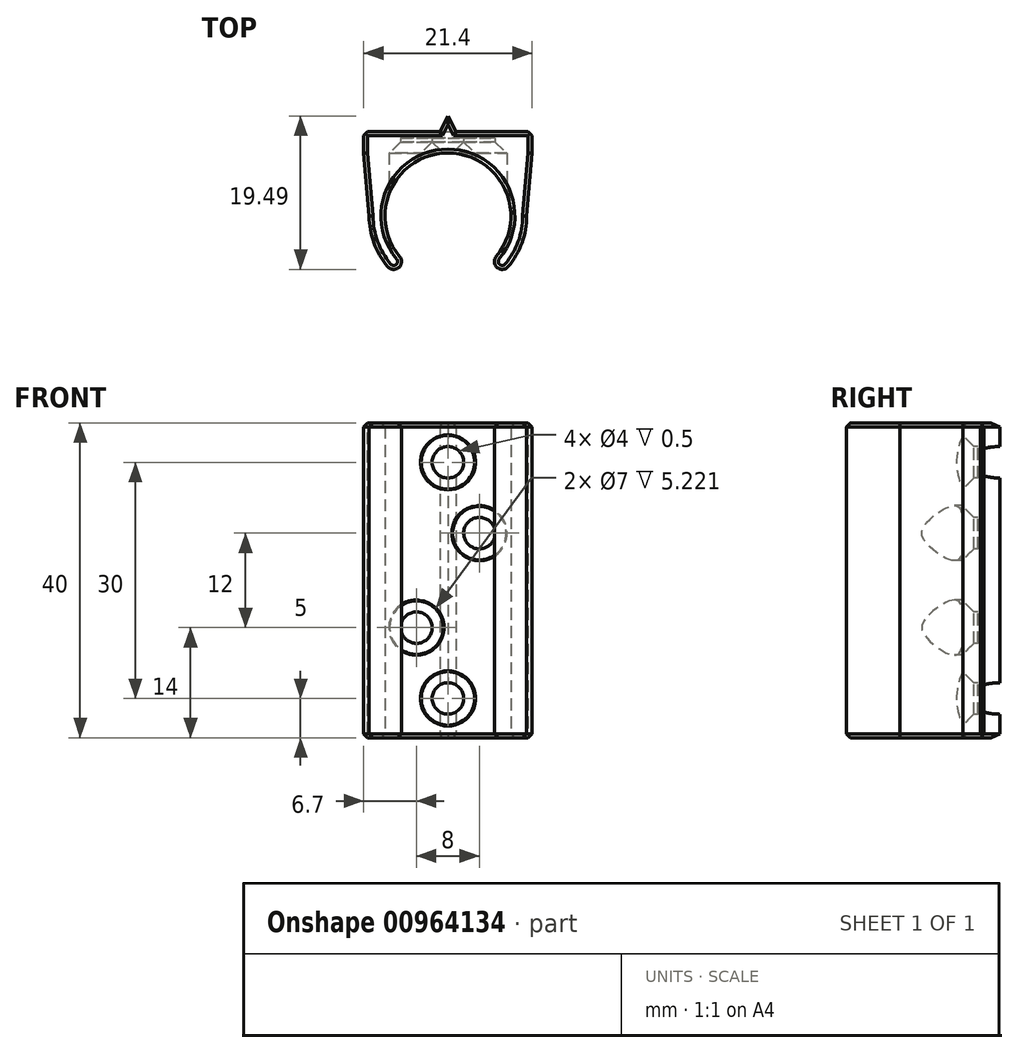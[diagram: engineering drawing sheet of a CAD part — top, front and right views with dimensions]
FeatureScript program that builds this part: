
annotation { "Feature Type Name" : "Feature", "Feature Type Description" : "" }
export const myFeature = defineFeature(function(context is Context, id is Id, definition is map)
    precondition{}
    {
        {
            var Q0;
            Q0=qCreatedBy(makeId("Top.planeOp"),FACE);
            var sketch = newSketch(context, id + "F0", { "sketchPlane" : qUnion([Q0])});
            skLineSegment(sketch, "E0", {"start": v(-10.7, 10.7) * mm, "end": v(-1, 10.7) * mm});
            skLineSegment(sketch, "E1", {"start": v(10.7, 10.7) * mm, "end": v(10.7, 8) * mm});
            skLineSegment(sketch, "E2", {"start": v(-10.7, 10.7) * mm, "end": v(-10.7, 8) * mm});
            skLineSegment(sketch, "E3", {"start": v(-1, 10.7) * mm, "end": v(0, 12.7) * mm});
            skLineSegment(sketch, "E4", {"start": v(0, 12.7) * mm, "end": v(1, 10.7) * mm});
            skLineSegment(sketch, "E5.trimOffspring", {"start": v(1, 10.7) * mm, "end": v(10.7, 10.7) * mm});
            skLineSegment(sketch, "E6", {"start": v(-8.05, -0.92) * mm, "end": v(-8.05, -0.92) * mm});
            skPoint(sketch, "E7.visualSharp", {"position": v(-10.7, 10.7) * mm});
            skPoint(sketch, "E8.visualSharp", {"position": v(10.7, 10.7) * mm});
            skLineSegment(sketch, "E9", {"start": v(0, 0) * mm, "end": v(-19.15, -16.07) * mm, "construction": true});
            skLineSegment(sketch, "E10", {"start": v(0, 0) * mm, "end": v(19.15, -16.07) * mm, "construction": true});
            skLineSegment(sketch, "E11", {"start": v(0, 0) * mm, "end": v(0, -25) * mm, "construction": true});
            skArc(sketch, "E12", {"start": v(6.13, -5.14) * mm, "mid": v(0, 8) * mm, "end": v(-6.13, -5.14) * mm});
            skArc(sketch, "E13", {"start": v(-10, 0) * mm, "mid": v(-9.4, -3.42) * mm, "end": v(-7.66, -6.43) * mm});
            skLineSegment(sketch, "E14", {"start": v(-10.7, 8) * mm, "end": v(-10, 0) * mm});
            skLineSegment(sketch, "E15", {"start": v(10.7, 8) * mm, "end": v(10, 0) * mm});
            skArc(sketch, "E16.trimOffspring", {"start": v(7.66, -6.43) * mm, "mid": v(9.4, -3.42) * mm, "end": v(10, 0) * mm});
            skArc(sketch, "E17", {"start": v(-6.13, -5.14) * mm, "mid": v(-6.25, -6.55) * mm, "end": v(-7.66, -6.43) * mm});
            skArc(sketch, "E18", {"start": v(6.13, -5.14) * mm, "mid": v(6.25, -6.55) * mm, "end": v(7.66, -6.43) * mm});
            skSolve(sketch);
        }
        {
            var Q0;
            Q0 = qSketchRegion(id + "F0", true);
            extrude(context, id + "F1", {"entities" : qUnion([Q0]), "endBound" : BoundingType.SYMMETRIC, "depth" : 40 * mm, "offsetDistance" : 25 * mm});
        }
        {
            var Q0;
            Q0=qCreatedBy(makeId("Front.planeOp"),FACE);
            cPlane(context, id + "F2", {"entities" : qUnion([Q0]), "cplaneType" : CPlaneType.OFFSET, "offset" : 10.7 * mm, "oppositeDirection" : true, "width" : 150 * mm, "height" : 150 * mm});
        }
        {
            var Q0;
            Q0=qCreatedBy(makeId("Front.planeOp"),FACE);
            var sketch = newSketch(context, id + "F3", { "sketchPlane" : qUnion([Q0])});
            skCircle(sketch, "E19", {"center": v(0, 15) * mm, "radius": 2 * mm});
            skCircle(sketch, "E20", {"center": v(0, -15) * mm, "radius": 2 * mm});
            skCircle(sketch, "E21", {"center": v(4, 6) * mm, "radius": 2 * mm});
            skCircle(sketch, "E22", {"center": v(-4, -6) * mm, "radius": 2 * mm});
            skSolve(sketch);
        }
        {
            var Q0;
            Q0 = qSketchRegion(id + "F3", true);
            extrude(context, id + "F4", {"entities" : qUnion([Q0]), "operationType" : NewBodyOperationType.REMOVE, "oppositeDirection" : true, "depth" : 9.9 * mm, "offsetDistance" : 25 * mm});
        }
        {
            var Q0;
            Q0=qCreatedBy(makeId("Front.planeOp"),FACE);
            var sketch = newSketch(context, id + "F5", { "sketchPlane" : qUnion([Q0])});
            skCircle(sketch, "E23", {"center": v(0, 15) * mm, "radius": 3.5 * mm});
            skCircle(sketch, "E24", {"center": v(4, 6) * mm, "radius": 3.5 * mm});
            skCircle(sketch, "E25", {"center": v(-4, -6) * mm, "radius": 3.5 * mm});
            skCircle(sketch, "E26", {"center": v(0, -15) * mm, "radius": 3.5 * mm});
            skSolve(sketch);
        }
        {
            var Q0;
            Q0 = qSketchRegion(id + "F5", true);
            extrude(context, id + "F6", {"entities" : qUnion([Q0]), "operationType" : NewBodyOperationType.REMOVE, "oppositeDirection" : true, "depth" : 8 * mm, "offsetDistance" : 25 * mm});
        }
        {
            var Q0;
            Q0=makeQuery(id+"F6.boolean.opBoolean","INTERSECT",EDGE,{"derivedFrom":[makeQuery(id+"F4.boolean.opBoolean","COPY",FACE,{"derivedFrom":makeQuery(id+"F4.opExtrude","SWEPT_FACE",FACE,{"disambiguationData":[OSD([sQuery(id+"F3.wireOp",EDGE,"E19")])]})}),makeQuery(id+"F6.opExtrude","CAP_FACE",FACE,{"disambiguationData":[OSD([sQuery(id+"F5.wireOp",EDGE,"E23")])],"isStart":false})]});
            var Q1;
            Q1=makeQuery(id+"F6.boolean.opBoolean","INTERSECT",EDGE,{"derivedFrom":[makeQuery(id+"F4.boolean.opBoolean","COPY",FACE,{"derivedFrom":makeQuery(id+"F4.opExtrude","SWEPT_FACE",FACE,{"disambiguationData":[OSD([sQuery(id+"F3.wireOp",EDGE,"E22")])]})}),makeQuery(id+"F6.opExtrude","CAP_FACE",FACE,{"disambiguationData":[OSD([sQuery(id+"F5.wireOp",EDGE,"E25")])],"isStart":false})]});
            var Q2;
            Q2=makeQuery(id+"F6.boolean.opBoolean","INTERSECT",EDGE,{"derivedFrom":[makeQuery(id+"F4.boolean.opBoolean","COPY",FACE,{"derivedFrom":makeQuery(id+"F4.opExtrude","SWEPT_FACE",FACE,{"disambiguationData":[OSD([sQuery(id+"F3.wireOp",EDGE,"E21")])]})}),makeQuery(id+"F6.opExtrude","CAP_FACE",FACE,{"disambiguationData":[OSD([sQuery(id+"F5.wireOp",EDGE,"E24")])],"isStart":false})]});
            var Q3;
            Q3=makeQuery(id+"F6.boolean.opBoolean","INTERSECT",EDGE,{"derivedFrom":[makeQuery(id+"F4.boolean.opBoolean","COPY",FACE,{"derivedFrom":makeQuery(id+"F4.opExtrude","SWEPT_FACE",FACE,{"disambiguationData":[OSD([sQuery(id+"F3.wireOp",EDGE,"E20")])]})}),makeQuery(id+"F6.opExtrude","CAP_FACE",FACE,{"disambiguationData":[OSD([sQuery(id+"F5.wireOp",EDGE,"E26")])],"isStart":false})]});
            chamfer(context, id + "F7", {"entities" : qUnion([Q0, Q1, Q2, Q3]), "width" : 1.4 * mm, "tangentPropagation" : true});
        }
        {
            var Q0;
            Q0=makeQuery(id+"F1.opExtrude","CAP_EDGE",EDGE,{"disambiguationData":[OSD([sQuery(id+"F0.wireOp",EDGE,"E13")])],"isStart":true});
            var Q1;
            Q1=makeQuery(id+"F1.opExtrude","CAP_EDGE",EDGE,{"disambiguationData":[OSD([sQuery(id+"F0.wireOp",EDGE,"E12")])],"isStart":true});
            var Q2;
            Q2=makeQuery(id+"F1.opExtrude","CAP_EDGE",EDGE,{"disambiguationData":[OSD([sQuery(id+"F0.wireOp",EDGE,"E14")])],"isStart":true});
            var Q3;
            Q3=makeQuery(id+"F1.opExtrude","CAP_EDGE",EDGE,{"disambiguationData":[OSD([sQuery(id+"F0.wireOp",EDGE,"E0")])],"isStart":true});
            var Q4;
            Q4=makeQuery(id+"F1.opExtrude","CAP_EDGE",EDGE,{"disambiguationData":[OSD([sQuery(id+"F0.wireOp",EDGE,"E5.trimOffspring")])],"isStart":true});
            var Q5;
            Q5=makeQuery(id+"F1.opExtrude","CAP_EDGE",EDGE,{"disambiguationData":[OSD([sQuery(id+"F0.wireOp",EDGE,"E4")])],"isStart":true});
            var Q6;
            Q6=makeQuery(id+"F1.opExtrude","CAP_EDGE",EDGE,{"disambiguationData":[OSD([sQuery(id+"F0.wireOp",EDGE,"E3")])],"isStart":true});
            var Q7;
            Q7=makeQuery(id+"F1.opExtrude","CAP_EDGE",EDGE,{"disambiguationData":[OSD([sQuery(id+"F0.wireOp",EDGE,"E2")])],"isStart":true});
            var Q8;
            Q8=makeQuery(id+"F1.opExtrude","CAP_EDGE",EDGE,{"disambiguationData":[OSD([sQuery(id+"F0.wireOp",EDGE,"E17")])],"isStart":true});
            var Q9;
            Q9=makeQuery(id+"F1.opExtrude","CAP_EDGE",EDGE,{"disambiguationData":[OSD([sQuery(id+"F0.wireOp",EDGE,"E18")])],"isStart":true});
            var Q10;
            Q10=makeQuery(id+"F1.opExtrude","CAP_EDGE",EDGE,{"disambiguationData":[OSD([sQuery(id+"F0.wireOp",EDGE,"E16.trimOffspring")])],"isStart":true});
            var Q11;
            Q11=makeQuery(id+"F1.opExtrude","CAP_EDGE",EDGE,{"disambiguationData":[OSD([sQuery(id+"F0.wireOp",EDGE,"E15")])],"isStart":true});
            var Q12;
            Q12=makeQuery(id+"F1.opExtrude","CAP_EDGE",EDGE,{"disambiguationData":[OSD([sQuery(id+"F0.wireOp",EDGE,"E1")])],"isStart":true});
            var Q13;
            Q13=makeQuery(id+"F1.opExtrude","CAP_FACE",FACE,{"disambiguationData":[OSD([sQuery(id+"F0.wireOp",EDGE,"E0"),sQuery(id+"F0.wireOp",EDGE,"E1"),sQuery(id+"F0.wireOp",EDGE,"E2"),sQuery(id+"F0.wireOp",EDGE,"E3"),sQuery(id+"F0.wireOp",EDGE,"E4"),sQuery(id+"F0.wireOp",EDGE,"E5.trimOffspring"),sQuery(id+"F0.wireOp",EDGE,"E12"),sQuery(id+"F0.wireOp",EDGE,"E13"),sQuery(id+"F0.wireOp",EDGE,"E14"),sQuery(id+"F0.wireOp",EDGE,"E15"),sQuery(id+"F0.wireOp",EDGE,"E16.trimOffspring"),sQuery(id+"F0.wireOp",EDGE,"E17"),sQuery(id+"F0.wireOp",EDGE,"E18")])],"isStart":false});
            chamfer(context, id + "F8", {"entities" : qUnion([Q0, Q1, Q2, Q3, Q4, Q5, Q6, Q7, Q8, Q9, Q10, Q11, Q12, Q13]), "width" : .5 * mm, "tangentPropagation" : true});
        }
        {
            var Q0;
            Q0=makeQuery(id+"F1.opExtrude","SWEPT_EDGE",EDGE,{"disambiguationData":[OSD([sQuery(id+"F0.wireOp",EDGE,"E1"),sQuery(id+"F0.wireOp",EDGE,"E5.trimOffspring")])]});
            var Q1;
            Q1=makeQuery(id+"F1.opExtrude","SWEPT_EDGE",EDGE,{"disambiguationData":[OSD([sQuery(id+"F0.wireOp",EDGE,"E0"),sQuery(id+"F0.wireOp",EDGE,"E2")])]});
            chamfer(context, id + "F9", {"entities" : qUnion([Q0, Q1]), "width" : .5 * mm, "tangentPropagation" : true});
        }
        {
            var Q0;
            Q0=qCreatedBy(id+"F2.planeOp",FACE);
            var sketch = newSketch(context, id + "F10", { "sketchPlane" : qUnion([Q0])});
            skCircle(sketch, "E27", {"center": v(0, 15) * mm, "radius": 2 * mm});
            skCircle(sketch, "E28", {"center": v(0, -15) * mm, "radius": 2 * mm});
            skCircle(sketch, "E29", {"center": v(4, 6) * mm, "radius": 2 * mm});
            skCircle(sketch, "E30", {"center": v(-4, -6) * mm, "radius": 2 * mm});
            skSolve(sketch);
        }
        {
            var Q0;
            Q0 = qSketchRegion(id + "F10", true);
            extrude(context, id + "F11", {"entities" : qUnion([Q0]), "operationType" : NewBodyOperationType.REMOVE, "oppositeDirection" : true, "depth" : 2 * mm, "offsetDistance" : 25 * mm});
        }
    });
